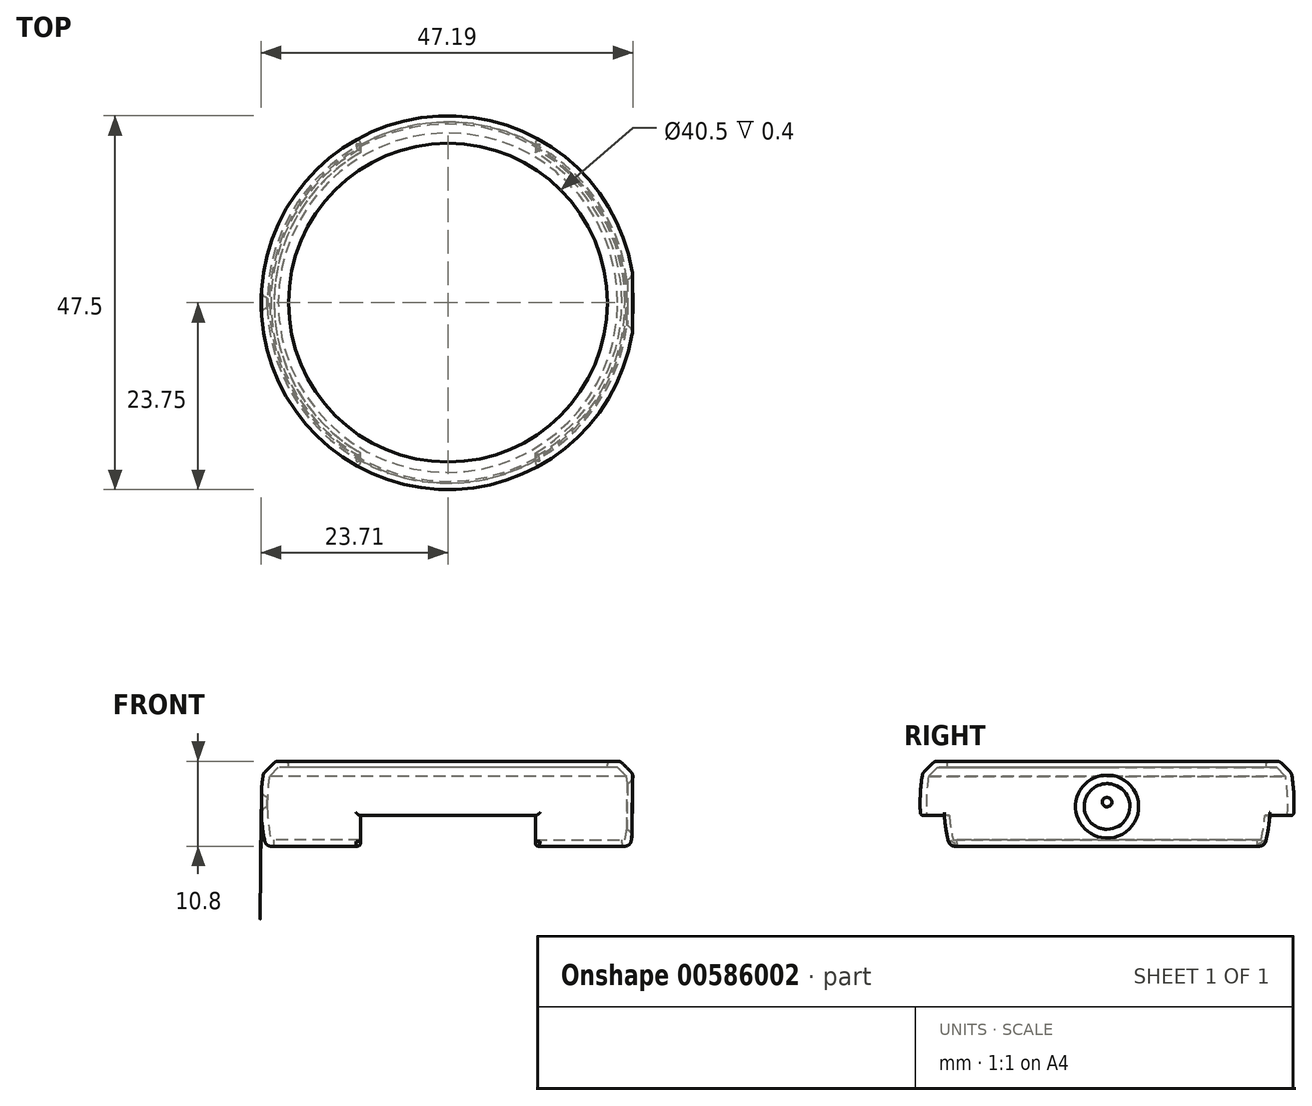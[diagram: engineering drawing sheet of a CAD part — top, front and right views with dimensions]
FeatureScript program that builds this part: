
annotation { "Feature Type Name" : "Feature", "Feature Type Description" : "" }
export const myFeature = defineFeature(function(context is Context, id is Id, definition is map)
    precondition{}
    {
        {
            var Q0;
            Q0=qCreatedBy(makeId("Front.planeOp"),FACE);
            var sketch = newSketch(context, id + "F0", { "sketchPlane" : qUnion([Q0])});
            skLineSegment(sketch, "E0", {"start": v(0, 0) * mm, "end": v(22.95, 0) * mm});
            skLineSegment(sketch, "E1", {"start": v(22.95, 0) * mm, "end": v(22.95, 0) * mm});
            skLineSegment(sketch, "E2", {"start": v(0, 4.6) * mm, "end": v(0, 0) * mm});
            skLineSegment(sketch, "E3", {"start": v(0, 4.6) * mm, "end": v(20.25, 4.6) * mm});
            skLineSegment(sketch, "E4", {"start": v(20.25, 4.6) * mm, "end": v(21.55, 4.6) * mm});
            skLineSegment(sketch, "E5", {"start": v(21.55, 4.6) * mm, "end": v(22.69, 3.46) * mm});
            skArc(sketch, "E6", {"start": v(22.95, 0) * mm, "mid": v(22.88, 1.74) * mm, "end": v(22.69, 3.46) * mm});
            skLineSegment(sketch, "E7", {"start": v(22.95, 0) * mm, "end": v(23.75, 0) * mm});
            skArc(sketch, "E8", {"start": v(23.75, 0) * mm, "mid": v(23.68, 1.8) * mm, "end": v(23.48, 3.58) * mm});
            skLineSegment(sketch, "E9", {"start": v(22.69, 3.46) * mm, "end": v(23.48, 3.58) * mm});
            skLineSegment(sketch, "E10.MirrorCS", {"start": v(0, 0) * mm, "end": v(-22.95, 0) * mm});
            skLineSegment(sketch, "E11.MirrorCS", {"start": v(0, -4.6) * mm, "end": v(0, 0) * mm});
            skLineSegment(sketch, "E12", {"start": v(0, -4.6) * mm, "end": v(22.08, -4.6) * mm});
            skLineSegment(sketch, "E13", {"start": v(22.08, -4.6) * mm, "end": v(22.48, -4.6) * mm});
            skArc(sketch, "E14", {"start": v(22.95, 0) * mm, "mid": v(22.83, -2.31) * mm, "end": v(22.48, -4.6) * mm});
            skLineSegment(sketch, "E15", {"start": v(22.48, -4.6) * mm, "end": v(23.27, -4.76) * mm});
            skArc(sketch, "E16", {"start": v(23.75, 0) * mm, "mid": v(23.63, -2.4) * mm, "end": v(23.27, -4.76) * mm});
            skLineSegment(sketch, "E17", {"start": v(21.55, 4.6) * mm, "end": v(22.12, 5.17) * mm});
            skLineSegment(sketch, "E18", {"start": v(22.12, 5.17) * mm, "end": v(23.25, 4.03) * mm});
            skLineSegment(sketch, "E19", {"start": v(23.25, 4.03) * mm, "end": v(22.69, 3.46) * mm});
            skArc(sketch, "E20", {"start": v(23.25, 4.03) * mm, "mid": v(23.4, 3.82) * mm, "end": v(23.48, 3.58) * mm});
            skLineSegment(sketch, "E21", {"start": v(20.25, 4.6) * mm, "end": v(20.25, 5.4) * mm});
            skLineSegment(sketch, "E22", {"start": v(20.25, 5.4) * mm, "end": v(21.55, 5.4) * mm});
            skLineSegment(sketch, "E23", {"start": v(21.55, 5.4) * mm, "end": v(21.55, 4.6) * mm});
            skArc(sketch, "E24", {"start": v(21.55, 5.4) * mm, "mid": v(21.86, 5.34) * mm, "end": v(22.12, 5.17) * mm});
            skLineSegment(sketch, "E25", {"start": v(22.08, -4.6) * mm, "end": v(22.08, -5.4) * mm});
            skLineSegment(sketch, "E26", {"start": v(22.08, -5.4) * mm, "end": v(22.48, -5.4) * mm});
            skLineSegment(sketch, "E27", {"start": v(22.48, -5.4) * mm, "end": v(22.48, -4.6) * mm});
            skArc(sketch, "E28", {"start": v(23.27, -4.76) * mm, "mid": v(23, -5.22) * mm, "end": v(22.48, -5.4) * mm});
            skSolve(sketch);
        }
        {
            var Q0;
            Q0=makeQuery(id+"F0.imprint","IMPRINT",FACE,{"disambiguationData":[TD([[makeQuery(id+"F0.imprint","IMPRINT",EDGE,{"derivedFrom":sQuery(id+"F0.wireOp",EDGE,"E4")}),1.0]])]});
            var Q1;
            Q1=makeQuery(id+"F0.imprint","IMPRINT",FACE,{"disambiguationData":[TD([[makeQuery(id+"F0.imprint","IMPRINT",EDGE,{"derivedFrom":sQuery(id+"F0.wireOp",EDGE,"E17")}),1.0]])]});
            var Q2;
            Q2=makeQuery(id+"F0.imprint","IMPRINT",FACE,{"disambiguationData":[TD([[makeQuery(id+"F0.imprint","IMPRINT",EDGE,{"derivedFrom":sQuery(id+"F0.wireOp",EDGE,"E5")}),1.0]])]});
            var Q3;
            Q3=makeQuery(id+"F0.imprint","IMPRINT",FACE,{"disambiguationData":[TD([[makeQuery(id+"F0.imprint","IMPRINT",EDGE,{"derivedFrom":sQuery(id+"F0.wireOp",EDGE,"E9")}),1.0]])]});
            var Q4;
            Q4=makeQuery(id+"F0.imprint","IMPRINT",FACE,{"disambiguationData":[TD([[makeQuery(id+"F0.imprint","IMPRINT",EDGE,{"derivedFrom":sQuery(id+"F0.wireOp",EDGE,"E6")}),-1.0]])]});
            var Q5;
            Q5=makeQuery(id+"F0.imprint","IMPRINT",FACE,{"disambiguationData":[TD([[makeQuery(id+"F0.imprint","IMPRINT",EDGE,{"derivedFrom":sQuery(id+"F0.wireOp",EDGE,"E7")}),-1.0]])]});
            var Q6;
            Q6=makeQuery(id+"F0.imprint","IMPRINT",FACE,{"disambiguationData":[TD([[makeQuery(id+"F0.imprint","IMPRINT",EDGE,{"derivedFrom":sQuery(id+"F0.wireOp",EDGE,"E15")}),-1.0]])]});
            var Q7;
            Q7=makeQuery(id+"F0.imprint","IMPRINT",FACE,{"disambiguationData":[TD([[makeQuery(id+"F0.imprint","IMPRINT",EDGE,{"derivedFrom":sQuery(id+"F0.wireOp",EDGE,"E13")}),-1.0]])]});
            var Q8;
            Q8=sQuery(id+"F0.wireOp",EDGE,"E2");
            revolve(context, id + "F1", {"entities" : qUnion([Q0, Q1, Q2, Q3, Q4, Q5, Q6, Q7]), "axis" : qUnion([Q8]), "revolveType" : RevolveType.FULL});
        }
        {
            var Q0;
            Q0=qCreatedBy(makeId("Right.planeOp"),FACE);
            var sketch = newSketch(context, id + "F2", { "sketchPlane" : qUnion([Q0])});
            skCircle(sketch, "E29", {"center": v(0, -0.35) * mm, "radius": 2.9 * mm});
            skLineSegment(sketch, "E30", {"start": v(0, -4.76) * mm, "end": v(0, 2.55) * mm});
            skSolve(sketch);
        }
        {
            var Q0;
            {var subQ0=sQuery(id+"F2.wireOp",EDGE,"hYWlRNpb-Yn6z-5j3d-uXe2-CcfcT86nRU5Y");var subQ1=sQuery(id+"F2.wireOp",EDGE,"E29");var subQ2=makeQuery(id+"F2.imprint","INTERSECT",VERTEX,{"disambiguationData":[OD(0.0)],"derivedFrom":[subQ1,subQ0]});Q0=makeQuery(id+"F2.imprint","IMPRINT",FACE,{"disambiguationData":[TD([[makeQuery(id+"F2.imprint","IMPRINT",EDGE,{"disambiguationData":[TD([[subQ2,1.0]])],"derivedFrom":subQ1}),1.0]])]});}
            var Q1;
            {var subQ0=sQuery(id+"F2.wireOp",EDGE,"hYWlRNpb-Yn6z-5j3d-uXe2-CcfcT86nRU5Y");var subQ1=sQuery(id+"F2.wireOp",EDGE,"E29");var subQ2=makeQuery(id+"F2.imprint","INTERSECT",VERTEX,{"disambiguationData":[OD(0.0)],"derivedFrom":[subQ1,subQ0]});Q1=makeQuery(id+"F2.imprint","IMPRINT",FACE,{"disambiguationData":[TD([[makeQuery(id+"F2.imprint","IMPRINT",EDGE,{"disambiguationData":[TD([[subQ2,-1.0]])],"derivedFrom":subQ1}),1.0]])]});}
            extrude(context, id + "F3", {"entities" : qUnion([Q0, Q1]), "operationType" : NewBodyOperationType.REMOVE, "endBound" : BoundingType.THROUGH_ALL, "depth" : -25 * mm, "offsetDistance" : 25 * mm});
        }
        {
            var Q0;
            Q0=qCreatedBy(makeId("Front.planeOp"),FACE);
            var sketch = newSketch(context, id + "F4", { "sketchPlane" : qUnion([Q0])});
            skLineSegment(sketch, "E31", {"start": v(0, -5.4) * mm, "end": v(11.1, -5.4) * mm});
            skLineSegment(sketch, "E32", {"start": v(11.1, -1.5) * mm, "end": v(0, -1.5) * mm});
            skLineSegment(sketch, "E33", {"start": v(0, -1.5) * mm, "end": v(0, -5.4) * mm});
            skLineSegment(sketch, "E34", {"start": v(11.1, -1.5) * mm, "end": v(11.1, -5.4) * mm});
            skLineSegment(sketch, "E35.MirrorCS", {"start": v(0, -5.4) * mm, "end": v(-11.1, -5.4) * mm});
            skLineSegment(sketch, "E36.MirrorCS", {"start": v(-11.1, -1.5) * mm, "end": v(0, -1.5) * mm});
            skLineSegment(sketch, "E37.MirrorCS", {"start": v(-11.1, -1.5) * mm, "end": v(-11.1, -5.4) * mm});
            skSolve(sketch);
        }
        {
            var Q0;
            Q0 = qSketchRegion(id + "F4", true);
            extrude(context, id + "F5", {"entities" : qUnion([Q0]), "operationType" : NewBodyOperationType.REMOVE, "endBound" : BoundingType.THROUGH_ALL, "oppositeDirection" : true, "depth" : 25 * mm, "offsetDistance" : 25 * mm});
        }
        {
            var Q0;
            Q0=makeQuery(id+"F4.imprint","IMPRINT",FACE,{"disambiguationData":[TD([[makeQuery(id+"F4.imprint","IMPRINT",EDGE,{"derivedFrom":sQuery(id+"F4.wireOp",EDGE,"E33")}),-1.0]])]});
            var Q1;
            Q1=makeQuery(id+"F4.imprint","IMPRINT",FACE,{"disambiguationData":[TD([[makeQuery(id+"F4.imprint","IMPRINT",EDGE,{"derivedFrom":sQuery(id+"F4.wireOp",EDGE,"E31")}),1.0]])]});
            extrude(context, id + "F6", {"entities" : qUnion([Q0, Q1]), "operationType" : NewBodyOperationType.REMOVE, "endBound" : BoundingType.THROUGH_ALL, "depth" : 25 * mm, "offsetDistance" : 25 * mm});
        }
        {
            var Q0;
            Q0=qCreatedBy(makeId("Right.planeOp"),FACE);
            var sketch = newSketch(context, id + "F7", { "sketchPlane" : qUnion([Q0])});
            skCircle(sketch, "E38", {"center": v(0, 0.2) * mm, "radius": 0.6 * mm});
            skSolve(sketch);
        }
        {
            var Q0;
            Q0=makeQuery(id+"F7.imprint","IMPRINT",FACE,{"disambiguationData":[TD([[makeQuery(id+"F7.imprint","IMPRINT",EDGE,{"derivedFrom":sQuery(id+"F7.wireOp",EDGE,"E38")}),1.0]])]});
            extrude(context, id + "F8", {"entities" : qUnion([Q0]), "operationType" : NewBodyOperationType.REMOVE, "endBound" : BoundingType.THROUGH_ALL, "oppositeDirection" : true, "depth" : 25 * mm, "offsetDistance" : 25 * mm});
        }
        {
            var Q0;
            Q0=makeQuery(id+"F1.opRevolve","SWEPT_EDGE",EDGE,{"disambiguationData":[OSD([sQuery(id+"F0.wireOp",EDGE,"E21"),sQuery(id+"F0.wireOp",EDGE,"E22")])]});
            var Q1;
            Q1=makeQuery(id+"F6.boolean.opBoolean","INTERSECT",EDGE,{"derivedFrom":[makeQuery(id+"F1.opRevolve","SWEPT_FACE",FACE,{"disambiguationData":[OSD([sQuery(id+"F0.wireOp",EDGE,"E8"),sQuery(id+"F0.wireOp",EDGE,"E16")])]}),makeQuery(id+"F6.opExtrude","SWEPT_FACE",FACE,{"disambiguationData":[OSD([sQuery(id+"F4.wireOp",EDGE,"E32"),sQuery(id+"F4.wireOp",EDGE,"E36.MirrorCS")])]})]});
            var Q2;
            {var subQ0=sQuery(id+"F0.wireOp",EDGE,"E25");var subQ1=sQuery(id+"F0.wireOp",EDGE,"E26");var subQ2=sQuery(id+"F4.wireOp",EDGE,"E34");Q2=makeQuery(id+"F6.boolean.opBoolean","SPLIT",EDGE,{"disambiguationData":[TD([makeQuery(id+"F5.boolean.opBoolean","COPY",FACE,{"derivedFrom":makeQuery(id+"F5.opExtrude","SWEPT_FACE",FACE,{"disambiguationData":[OSD([subQ2])]})})])],"derivedFrom":makeQuery(id+"F1.opRevolve","SWEPT_EDGE",EDGE,{"disambiguationData":[OSD([subQ0,subQ1])]})});}
            var Q3;
            Q3=makeQuery(id+"F5.boolean.opBoolean","INTERSECT",EDGE,{"derivedFrom":[makeQuery(id+"F1.opRevolve","SWEPT_FACE",FACE,{"disambiguationData":[OSD([sQuery(id+"F0.wireOp",EDGE,"E8"),sQuery(id+"F0.wireOp",EDGE,"E16")])]}),makeQuery(id+"F5.opExtrude","SWEPT_FACE",FACE,{"disambiguationData":[OSD([sQuery(id+"F4.wireOp",EDGE,"E32"),sQuery(id+"F4.wireOp",EDGE,"E36.MirrorCS")])]})]});
            var Q4;
            Q4=makeQuery(id+"F6.boolean.opBoolean","INTERSECT",EDGE,{"derivedFrom":[makeQuery(id+"F1.opRevolve","SWEPT_FACE",FACE,{"disambiguationData":[OSD([sQuery(id+"F0.wireOp",EDGE,"E8"),sQuery(id+"F0.wireOp",EDGE,"E16")])]}),makeQuery(id+"F6.opExtrude","SWEPT_FACE",FACE,{"disambiguationData":[OSD([sQuery(id+"F4.wireOp",EDGE,"E34")])]})]});
            var Q5;
            Q5=makeQuery(id+"F6.boolean.opBoolean","INTERSECT",EDGE,{"derivedFrom":[makeQuery(id+"F1.opRevolve","SWEPT_FACE",FACE,{"disambiguationData":[OSD([sQuery(id+"F0.wireOp",EDGE,"E8"),sQuery(id+"F0.wireOp",EDGE,"E16")])]}),makeQuery(id+"F6.opExtrude","SWEPT_FACE",FACE,{"disambiguationData":[OSD([sQuery(id+"F4.wireOp",EDGE,"E37.MirrorCS")])]})]});
            var Q6;
            Q6=makeQuery(id+"F5.boolean.opBoolean","INTERSECT",EDGE,{"derivedFrom":[makeQuery(id+"F1.opRevolve","SWEPT_FACE",FACE,{"disambiguationData":[OSD([sQuery(id+"F0.wireOp",EDGE,"E8"),sQuery(id+"F0.wireOp",EDGE,"E16")])]}),makeQuery(id+"F5.opExtrude","SWEPT_FACE",FACE,{"disambiguationData":[OSD([sQuery(id+"F4.wireOp",EDGE,"E37.MirrorCS")])]})]});
            var Q7;
            Q7=makeQuery(id+"F5.boolean.opBoolean","INTERSECT",EDGE,{"derivedFrom":[makeQuery(id+"F1.opRevolve","SWEPT_FACE",FACE,{"disambiguationData":[OSD([sQuery(id+"F0.wireOp",EDGE,"E8"),sQuery(id+"F0.wireOp",EDGE,"E16")])]}),makeQuery(id+"F5.opExtrude","SWEPT_FACE",FACE,{"disambiguationData":[OSD([sQuery(id+"F4.wireOp",EDGE,"E34")])]})]});
            fillet(context, id + "F9", {"entities" : qUnion([Q0, Q1, Q2, Q3, Q4, Q5, Q6, Q7]), "radius" : 0.4 * mm, "tangentPropagation" : true, "allowEdgeOverflow" : false});
        }
        {
            var Q0;
            Q0=makeQuery(id+"F3.boolean.opBoolean","INTERSECT",EDGE,{"derivedFrom":[makeQuery(id+"F1.opRevolve","SWEPT_FACE",FACE,{"disambiguationData":[OSD([sQuery(id+"F0.wireOp",EDGE,"E8"),sQuery(id+"F0.wireOp",EDGE,"E16")])]}),makeQuery(id+"F3.opExtrude","SWEPT_FACE",FACE,{"disambiguationData":[OSD([sQuery(id+"F2.wireOp",EDGE,"E29")])]})]});
            var Q1;
            Q1=makeQuery(id+"F8.boolean.opBoolean","INTERSECT",EDGE,{"derivedFrom":[makeQuery(id+"F1.opRevolve","SWEPT_FACE",FACE,{"disambiguationData":[OSD([sQuery(id+"F0.wireOp",EDGE,"E8"),sQuery(id+"F0.wireOp",EDGE,"E16")])]}),makeQuery(id+"F8.opExtrude","SWEPT_FACE",FACE,{"disambiguationData":[OSD([sQuery(id+"F7.wireOp",EDGE,"E38")])]})]});
            fillet(context, id + "F10", {"entities" : qUnion([Q0, Q1]), "radius" : 1 * mm, "tangentPropagation" : true, "allowEdgeOverflow" : false});
        }
    });
